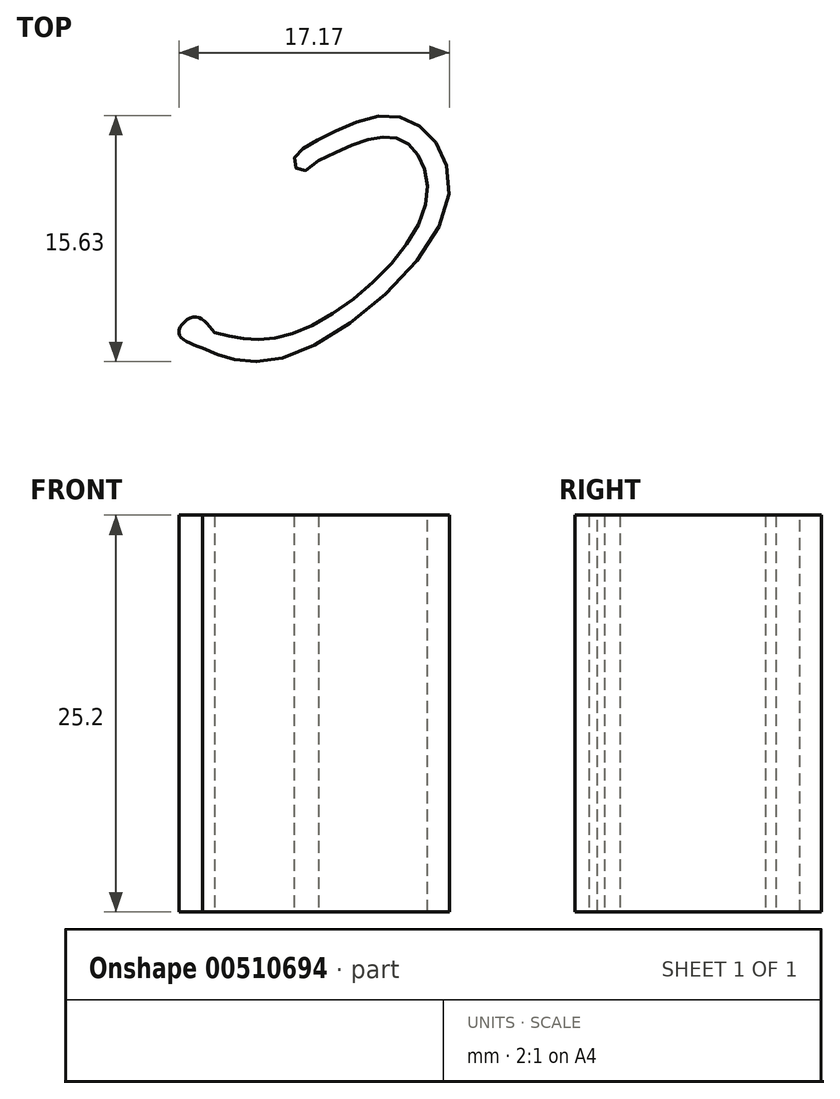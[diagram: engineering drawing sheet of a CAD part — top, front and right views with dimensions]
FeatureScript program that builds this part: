
annotation { "Feature Type Name" : "Feature", "Feature Type Description" : "" }
export const myFeature = defineFeature(function(context is Context, id is Id, definition is map)
    precondition{}
    {
        {
            var Q0;
            Q0=qCreatedBy(makeId("Top.planeOp"),FACE);
            var sketch = newSketch(context, id + "F0", { "sketchPlane" : qUnion([Q0])});
            skFitSpline(sketch, "E0", {"points": [v(0, 0) * mm, v(5.15, 0) * mm, v(13.33, 7.92) * mm, v(11.78, 12.27) * mm, v(6.58, 10.9) * mm], "startDerivative": vector(20.6, -5.06) * mm, "endDerivative": vector(-24.96, -12.56) * mm});
            skFitSpline(sketch, "E1", {"points": [v(-0.78, -0.98) * mm, v(1.1, -1.68) * mm, v(5.66, -1.13) * mm, v(14.52, 7.34) * mm, v(13.82, 12.36) * mm, v(11, 13.78) * mm, v(7.62, 12.76) * mm, v(5.58, 11.66) * mm, v(5.03, 10.9) * mm, v(5.42, 10.24) * mm, v(6.58, 10.9) * mm], "startDerivative": vector(21.2, -9.85) * mm, "endDerivative": vector(19.34, 16.96) * mm});
            skFitSpline(sketch, "E2", {"points": [v(0, 0) * mm, v(-1.33, 0.98) * mm, v(-2.27, 0) * mm, v(-0.78, -0.98) * mm], "startDerivative": vector(-3.68, 4.62) * mm, "endDerivative": vector(6.23, -2.24) * mm});
            skSolve(sketch);
        }
        {
            var Q0;
            Q0=makeQuery(id+"F0.imprint","IMPRINT",FACE,{"disambiguationData":[TD([[makeQuery(id+"F0.imprint","IMPRINT",EDGE,{"derivedFrom":sQuery(id+"F0.wireOp",EDGE,"E0")}),-1.0]])]});
            extrude(context, id + "F1", {"entities" : qUnion([Q0]), "depth" : 25.2 * mm});
        }
    });
